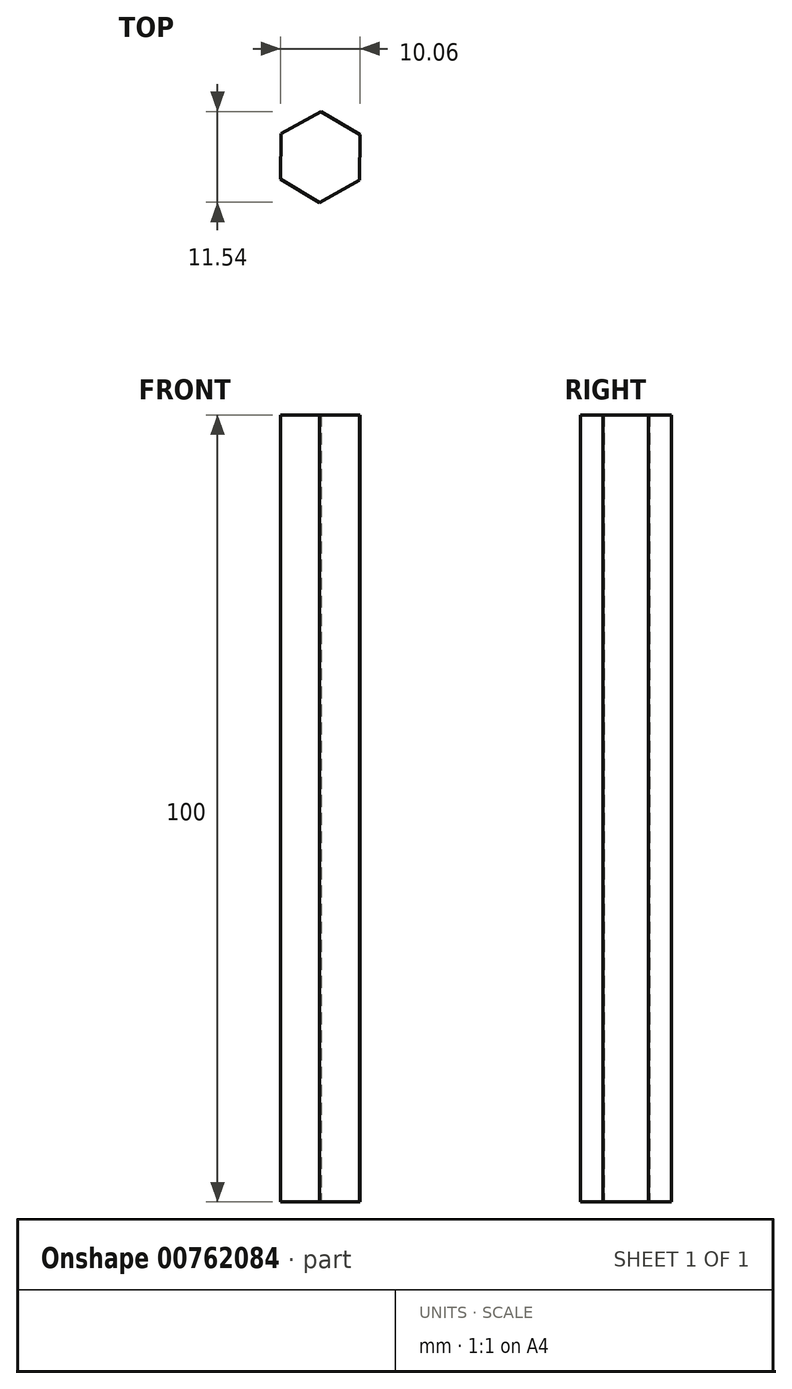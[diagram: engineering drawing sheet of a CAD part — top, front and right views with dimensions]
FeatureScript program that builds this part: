
annotation { "Feature Type Name" : "Feature", "Feature Type Description" : "" }
export const myFeature = defineFeature(function(context is Context, id is Id, definition is map)
    precondition{}
    {
        {
            var Q0;
            Q0=qCreatedBy(makeId("Top.planeOp"),FACE);
            var sketch = newSketch(context, id + "F0", { "sketchPlane" : qUnion([Q0])});
            skCircle(sketch, "E0.cCircle", {"center": v(0, 0) * mm, "radius": 5 * mm, "construction": true});
            skLineSegment(sketch, "E0.0", {"start": v(-4.96, 2.95) * mm, "end": v(0.07, 5.77) * mm});
            skLineSegment(sketch, "E0.1", {"start": v(0.07, 5.77) * mm, "end": v(5.03, 2.83) * mm});
            skLineSegment(sketch, "E0.2", {"start": v(5.03, 2.83) * mm, "end": v(4.96, -2.95) * mm});
            skLineSegment(sketch, "E0.3", {"start": v(4.96, -2.95) * mm, "end": v(-0.07, -5.77) * mm});
            skLineSegment(sketch, "E0.4", {"start": v(-0.07, -5.77) * mm, "end": v(-5.03, -2.83) * mm});
            skLineSegment(sketch, "E0.5", {"start": v(-5.03, -2.83) * mm, "end": v(-4.96, 2.95) * mm});
            skPoint(sketch, "E0.0.midPoint", {"position": v(-2.45, 4.36) * mm});
            skSolve(sketch);
        }
        {
            var Q0;
            Q0 = qSketchRegion(id + "F0", true);
            extrude(context, id + "F1", {"entities" : qUnion([Q0]), "depth" : 100 * mm, "offsetDistance" : 25 * mm});
        }
    });
